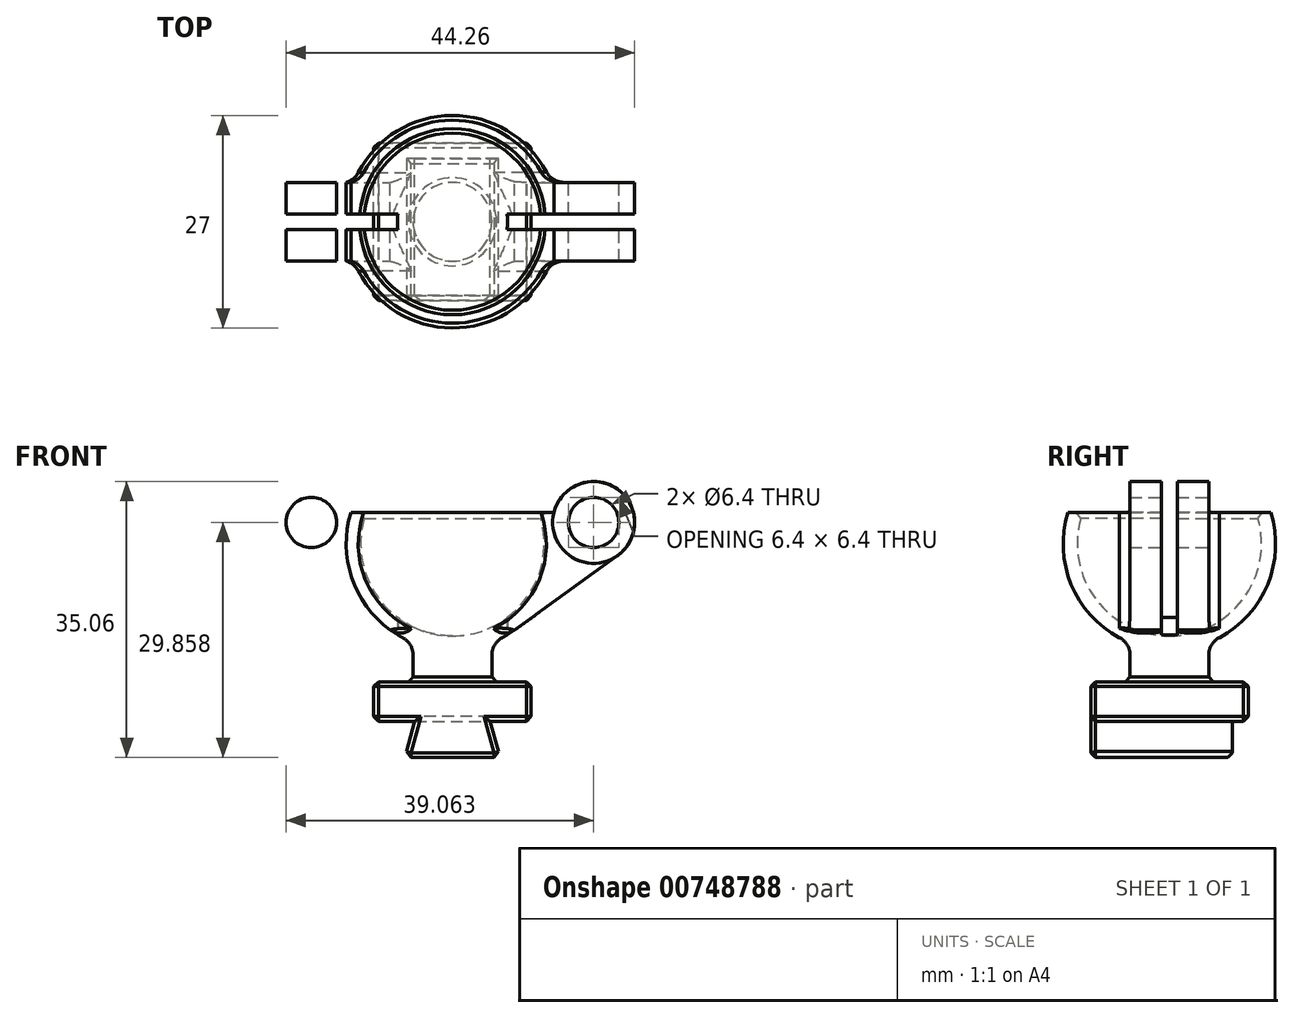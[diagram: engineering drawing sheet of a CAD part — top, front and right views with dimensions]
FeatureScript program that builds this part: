
annotation { "Feature Type Name" : "Feature", "Feature Type Description" : "" }
export const myFeature = defineFeature(function(context is Context, id is Id, definition is map)
    precondition{}
    {
        {
            assignVariable(context, id + "F0", {"name" : "BallWallThickness", "anyValue" : 2});
        }
        {
            assignVariable(context, id + "F1", {"name" : "DovetailBackstopDepth", "anyValue" : 2});
        }
        {
            assignVariable(context, id + "F2", {"name" : "DovetailHeight", "anyValue" : 5});
        }
        {
            assignVariable(context, id + "F3", {"name" : "Thickness", "anyValue" : 20});
        }
        {
            var Q0;
            Q0=qCreatedBy(makeId("Front.planeOp"),FACE);
            var sketch = newSketch(context, id + "F4", { "sketchPlane" : qUnion([Q0])});
            skLineSegment(sketch, "E0", {"start": v(20, 0) * mm, "end": v(20, 5) * mm});
            skLineSegment(sketch, "E1", {"start": v(20, 5) * mm, "end": v(0, 5) * mm});
            skLineSegment(sketch, "E2", {"start": v(5, 5) * mm, "end": v(5, 10) * mm});
            skLineSegment(sketch, "E3", {"start": v(5, 10) * mm, "end": v(15, 10) * mm});
            skLineSegment(sketch, "E4", {"start": v(15, 10) * mm, "end": v(15, 5) * mm});
            skLineSegment(sketch, "E5", {"start": v(10, 5) * mm, "end": v(10, -4.6) * mm, "construction": true});
            skArc(sketch, "E6", {"start": v(-2.9, 26.54) * mm, "mid": v(-2.18, 16.73) * mm, "end": v(5, 10) * mm});
            skPoint(sketch, "E6.centerSnap0", {"position": v(10, 10) * mm});
            skArc(sketch, "E7.trimOffspring", {"start": v(15, 10) * mm, "mid": v(22.18, 16.73) * mm, "end": v(22.9, 26.54) * mm});
            skLineSegment(sketch, "E8", {"start": v(10, 26.54) * mm, "end": v(10, 5) * mm});
            skArc(sketch, "E9", {"start": v(-1, 26.54) * mm, "mid": v(10, 10.84) * mm, "end": v(21, 26.54) * mm});
            skLineSegment(sketch, "E10", {"start": v(5.2, 0) * mm, "end": v(3.97, -4.6) * mm});
            skLineSegment(sketch, "E11", {"start": v(3.97, -4.6) * mm, "end": v(16.03, -4.6) * mm});
            skLineSegment(sketch, "E12.MirrorCS", {"start": v(14.8, 0) * mm, "end": v(16.03, -4.6) * mm});
            skLineSegment(sketch, "E13", {"start": v(14.8, 0) * mm, "end": v(20, 0) * mm});
            skLineSegment(sketch, "E14", {"start": v(5.2, 0) * mm, "end": v(0, 0) * mm});
            skLineSegment(sketch, "E15", {"start": v(0, 0) * mm, "end": v(0, 5) * mm});
            skLineSegment(sketch, "E16", {"start": v(-3.5, 22.54) * mm, "end": v(23.5, 22.54) * mm, "construction": true});
            skLineSegment(sketch, "E17", {"start": v(22.9, 26.54) * mm, "end": v(-2.9, 26.54) * mm});
            skLineSegment(sketch, "E18", {"start": v(5.2, 0) * mm, "end": v(14.8, 0) * mm});
            skCircle(sketch, "E19", {"center": v(27.93, 25.26) * mm, "radius": 3.2 * mm});
            skArc(sketch, "E20.0", {"start": v(30.98, 21.04) * mm, "mid": v(30.86, 29.56) * mm, "end": v(22.9, 26.54) * mm});
            skLineSegment(sketch, "E21", {"start": v(30.98, 21.04) * mm, "end": v(17.9, 11.6) * mm});
            skCircle(sketch, "E22.MirrorC", {"center": v(-7.93, 25.26) * mm, "radius": 3.2 * mm});
            skLineSegment(sketch, "E23.MirrorCS", {"start": v(-10.98, 21.04) * mm, "end": v(2.1, 11.6) * mm});
            skArc(sketch, "E24.MirrorCS", {"start": v(-10.98, 21.04) * mm, "mid": v(-10.86, 29.56) * mm, "end": v(-2.9, 26.54) * mm});
            skLineSegment(sketch, "E25", {"start": v(17.9, 11.6) * mm, "end": v(16.85, 13.06) * mm});
            skLineSegment(sketch, "E26.MirrorCS", {"start": v(2.1, 11.6) * mm, "end": v(3.15, 13.06) * mm});
            skSolve(sketch);
        }
        {
            var Q0;
            Q0=makeQuery(id+"F4.imprint","IMPRINT",FACE,{"disambiguationData":[TD([[makeQuery(id+"F4.imprint","IMPRINT",EDGE,{"derivedFrom":sQuery(id+"F4.wireOp",EDGE,"E10")}),1.0]])]});
            extrude(context, id + "F5", {"entities" : qUnion([Q0]), "depth" : (getVariable(context, 'Thickness') / 2) * mm, "hasSecondDirection" : true, "secondDirectionOppositeDirection" : true, "secondDirectionDepth" : (getVariable(context, 'Thickness') / 2 - getVariable(context, 'DovetailBackstopDepth')) * mm});
        }
        {
            var Q0;
            {var subQ4=sQuery(id+"F4.wireOp",EDGE,"E0");Q0=makeQuery(id+"F4.imprint","IMPRINT",FACE,{"disambiguationData":[TD([[makeQuery(id+"F4.imprint","IMPRINT",EDGE,{"derivedFrom":subQ4}),1.0]])]});}
            extrude(context, id + "F6", {"entities" : qUnion([Q0]), "operationType" : NewBodyOperationType.ADD, "depth" : (getVariable(context, 'Thickness')) * mm, "symmetric" : true});
        }
        {
            var Q0;
            {var subQ0=sQuery(id+"F4.wireOp",EDGE,"E2");Q0=makeQuery(id+"F4.imprint","IMPRINT",FACE,{"disambiguationData":[TD([[makeQuery(id+"F4.imprint","IMPRINT",EDGE,{"derivedFrom":subQ0}),-1.0]])]});}
            var Q1;
            Q1=sQuery(id+"F4.wireOp",EDGE,"E8");
            revolve(context, id + "F7", {"operationType" : NewBodyOperationType.ADD, "entities" : qUnion([Q0]), "axis" : qUnion([Q1]), "revolveType" : RevolveType.FULL});
        }
        {
            var Q0;
            Q0=makeQuery(id+"F7.opRevolve","SWEPT_FACE",FACE,{"disambiguationData":[OSD([sQuery(id+"F4.wireOp",EDGE,"E3")])]});
            var sketch = newSketch(context, id + "F8", { "sketchPlane" : qUnion([Q0])});
            skCircle(sketch, "E27", {"center": v(10, 0) * mm, "radius": 13.5 * mm});
            skCircle(sketch, "E28.0", {"center": v(10, 0) * mm, "radius": 5 * mm});
            skLineSegment(sketch, "E29", {"start": v(10, 13.5) * mm, "end": v(10, -13.5) * mm, "construction": true});
            skLineSegment(sketch, "E30", {"start": v(9.5, 13.5) * mm, "end": v(9.5, 6.98) * mm, "construction": true});
            skLineSegment(sketch, "E31.MirrorCS", {"start": v(10.5, 13.5) * mm, "end": v(10.5, 6.98) * mm, "construction": true});
            skLineSegment(sketch, "E32.trimOffspring", {"start": v(9.5, -6.98) * mm, "end": v(9.5, -13.5) * mm, "construction": true});
            skLineSegment(sketch, "E33.trimOffspring", {"start": v(10.5, -6.98) * mm, "end": v(10.5, -13.5) * mm, "construction": true});
            skLineSegment(sketch, "E34", {"start": v(-3.5, 0) * mm, "end": v(23.5, 0) * mm, "construction": true});
            skLineSegment(sketch, "E35", {"start": v(-3.46, 1) * mm, "end": v(3.07, 1) * mm});
            skLineSegment(sketch, "E36.MirrorCS", {"start": v(-3.46, -1) * mm, "end": v(3.07, -1) * mm});
            skLineSegment(sketch, "E37.trimOffspring", {"start": v(16.93, -1) * mm, "end": v(23.46, -1) * mm});
            skLineSegment(sketch, "E38.trimOffspring", {"start": v(16.93, 1) * mm, "end": v(23.46, 1) * mm});
            skCircle(sketch, "E39.0", {"center": v(10, 0) * mm, "radius": 7 * mm});
            skLineSegment(sketch, "E40", {"start": v(-3.46, -1) * mm, "end": v(-33.46, -1) * mm});
            skLineSegment(sketch, "E41", {"start": v(-33.46, -1) * mm, "end": v(-33.46, 1) * mm});
            skLineSegment(sketch, "E42", {"start": v(-33.46, 1) * mm, "end": v(-3.46, 1) * mm});
            skLineSegment(sketch, "E43.MirrorCS", {"start": v(53.46, 1) * mm, "end": v(23.46, 1) * mm});
            skLineSegment(sketch, "E44.MirrorCS", {"start": v(23.46, -1) * mm, "end": v(53.46, -1) * mm});
            skLineSegment(sketch, "E45.MirrorCS", {"start": v(53.46, -1) * mm, "end": v(53.46, 1) * mm});
            skSolve(sketch);
        }
        {
            var Q0;
            {var subQ6=sQuery(id+"F4.wireOp",EDGE,"E6");Q0=makeQuery(id+"F4.imprint","IMPRINT",FACE,{"disambiguationData":[TD([[makeQuery(id+"F4.imprint","IMPRINT",EDGE,{"derivedFrom":subQ6}),1.0]])]});}
            var Q1;
            {var subQ0=sQuery(id+"F4.wireOp",EDGE,"E26.MirrorCS");Q1=makeQuery(id+"F4.imprint","IMPRINT",FACE,{"disambiguationData":[TD([[makeQuery(id+"F4.imprint","IMPRINT",EDGE,{"derivedFrom":subQ0}),-1.0]])]});}
            var Q2;
            Q2=sQuery(id+"F4.wireOp",EDGE,"E8");
            revolve(context, id + "F9", {"operationType" : NewBodyOperationType.ADD, "entities" : qUnion([Q0, Q1]), "axis" : qUnion([Q2]), "revolveType" : RevolveType.FULL});
        }
        {
            var Q0;
            Q0=makeQuery(id+"F4.imprint","IMPRINT",FACE,{"disambiguationData":[TD([[makeQuery(id+"F4.imprint","IMPRINT",EDGE,{"derivedFrom":sQuery(id+"F4.wireOp",EDGE,"E22.MirrorC")}),1.0]])]});
            var Q1;
            {var subQ3=sQuery(id+"F4.wireOp",EDGE,"E26.MirrorCS");Q1=makeQuery(id+"F4.imprint","IMPRINT",FACE,{"disambiguationData":[TD([[makeQuery(id+"F4.imprint","IMPRINT",EDGE,{"derivedFrom":subQ3}),1.0]])]});}
            var Q2;
            {var subQ3=sQuery(id+"F4.wireOp",EDGE,"E25");Q2=makeQuery(id+"F4.imprint","IMPRINT",FACE,{"disambiguationData":[TD([[makeQuery(id+"F4.imprint","IMPRINT",EDGE,{"derivedFrom":subQ3}),-1.0]])]});}
            var Q3;
            Q3=makeQuery(id+"F4.imprint","IMPRINT",FACE,{"disambiguationData":[TD([[makeQuery(id+"F4.imprint","IMPRINT",EDGE,{"derivedFrom":sQuery(id+"F4.wireOp",EDGE,"E19")}),-1.0]])]});
            extrude(context, id + "F10", {"entities" : qUnion([Q0, Q1, Q2, Q3]), "operationType" : NewBodyOperationType.ADD, "depth" : (getVariable(context, 'BallWallThickness') + 8) * mm, "symmetric" : true});
        }
        {
            var Q0;
            {var subQ0=sQuery(id+"F8.wireOp",EDGE,"E35");Q0=makeQuery(id+"F8.imprint","IMPRINT",FACE,{"disambiguationData":[TD([[makeQuery(id+"F8.imprint","IMPRINT",EDGE,{"derivedFrom":subQ0}),-1.0]])]});}
            var Q1;
            {var subQ0=sQuery(id+"F8.wireOp",EDGE,"E32.trimOffspring");Q1=makeQuery(id+"F8.imprint","IMPRINT",FACE,{"disambiguationData":[TD([[makeQuery(id+"F8.imprint","IMPRINT",EDGE,{"derivedFrom":subQ0}),1.0]])]});}
            var Q2;
            {var subQ0=sQuery(id+"F8.wireOp",EDGE,"E37.trimOffspring");Q2=makeQuery(id+"F8.imprint","IMPRINT",FACE,{"disambiguationData":[TD([[makeQuery(id+"F8.imprint","IMPRINT",EDGE,{"derivedFrom":subQ0}),1.0]])]});}
            var Q3;
            {var subQ0=sQuery(id+"F8.wireOp",EDGE,"E30");Q3=makeQuery(id+"F8.imprint","IMPRINT",FACE,{"disambiguationData":[TD([[makeQuery(id+"F8.imprint","IMPRINT",EDGE,{"derivedFrom":subQ0}),1.0]])]});}
            var Q4;
            {var subQ2=sQuery(id+"F8.wireOp",EDGE,"E40");Q4=makeQuery(id+"F8.imprint","IMPRINT",FACE,{"disambiguationData":[TD([[makeQuery(id+"F8.imprint","IMPRINT",EDGE,{"derivedFrom":subQ2}),-1.0]])]});}
            var Q5;
            {var subQ2=sQuery(id+"F8.wireOp",EDGE,"E43.MirrorCS");Q5=makeQuery(id+"F8.imprint","IMPRINT",FACE,{"disambiguationData":[TD([[makeQuery(id+"F8.imprint","IMPRINT",EDGE,{"derivedFrom":subQ2}),1.0]])]});}
            extrude(context, id + "F11", {"entities" : qUnion([Q0, Q1, Q2, Q3, Q4, Q5]), "operationType" : NewBodyOperationType.REMOVE, "depth" : 25 * mm});
        }
        {
            var Q0;
            {var subQ0=sQuery(id+"F4.wireOp",EDGE,"E6");var subQ1=sQuery(id+"F4.wireOp",EDGE,"E3");var subQ2=sQuery(id+"F4.wireOp",EDGE,"E2");Q0=makeQuery(id+"F9.boolean.opBoolean","MERGE",EDGE,{"derivedFrom":[makeQuery(id+"F7.opRevolve","SWEPT_EDGE",EDGE,{"disambiguationData":[OSD([subQ2,subQ1,subQ0])]}),makeQuery(id+"F9.opRevolve","SWEPT_EDGE",EDGE,{"disambiguationData":[OSD([subQ2,subQ1,subQ0])]})]});}
            var Q1;
            Q1=makeQuery(id+"F7.opRevolve","SWEPT_EDGE",EDGE,{"disambiguationData":[OSD([sQuery(id+"F4.wireOp",EDGE,"E1"),sQuery(id+"F4.wireOp",EDGE,"E2")])]});
            var Q2;
            Q2=makeQuery(id+"F10.boolean.opBoolean","INTERSECT",EDGE,{"disambiguationData":[OD(1.0)],"derivedFrom":[makeQuery(id+"F9.opRevolve","SWEPT_FACE",FACE,{"disambiguationData":[OSD([sQuery(id+"F4.wireOp",EDGE,"E6")])]}),makeQuery(id+"F10.opExtrude","SWEPT_FACE",FACE,{"disambiguationData":[OSD([sQuery(id+"F4.wireOp",EDGE,"E26.MirrorCS")])]})]});
            var Q3;
            Q3=makeQuery(id+"F10.boolean.opBoolean","INTERSECT",EDGE,{"disambiguationData":[OD(1.0)],"derivedFrom":[makeQuery(id+"F9.opRevolve","SWEPT_FACE",FACE,{"disambiguationData":[OSD([sQuery(id+"F4.wireOp",EDGE,"E6")])]}),makeQuery(id+"F10.opExtrude","SWEPT_FACE",FACE,{"disambiguationData":[OSD([sQuery(id+"F4.wireOp",EDGE,"E25")])]})]});
            var Q4;
            Q4=makeQuery(id+"F10.boolean.opBoolean","INTERSECT",EDGE,{"disambiguationData":[OD(0.0)],"derivedFrom":[makeQuery(id+"F9.opRevolve","SWEPT_FACE",FACE,{"disambiguationData":[OSD([sQuery(id+"F4.wireOp",EDGE,"E6")])]}),makeQuery(id+"F10.opExtrude","SWEPT_FACE",FACE,{"disambiguationData":[OSD([sQuery(id+"F4.wireOp",EDGE,"E25")])]})]});
            var Q5;
            Q5=makeQuery(id+"F10.boolean.opBoolean","INTERSECT",EDGE,{"disambiguationData":[OD(0.0)],"derivedFrom":[makeQuery(id+"F9.opRevolve","SWEPT_FACE",FACE,{"disambiguationData":[OSD([sQuery(id+"F4.wireOp",EDGE,"E6")])]}),makeQuery(id+"F10.opExtrude","SWEPT_FACE",FACE,{"disambiguationData":[OSD([sQuery(id+"F4.wireOp",EDGE,"E26.MirrorCS")])]})]});
            var Q6;
            Q6=makeQuery(id+"F10.boolean.opBoolean","INTERSECT",EDGE,{"derivedFrom":[makeQuery(id+"F9.opRevolve","SWEPT_FACE",FACE,{"disambiguationData":[OSD([sQuery(id+"F4.wireOp",EDGE,"E6")])]}),makeQuery(id+"F10.opExtrude","CAP_FACE",FACE,{"disambiguationData":[OSD([sQuery(id+"F4.wireOp",EDGE,"E9"),sQuery(id+"F4.wireOp",EDGE,"E17"),sQuery(id+"F4.wireOp",EDGE,"E19"),sQuery(id+"F4.wireOp",EDGE,"E20.0"),sQuery(id+"F4.wireOp",EDGE,"E21"),sQuery(id+"F4.wireOp",EDGE,"E25")])],"isStart":false})]});
            var Q7;
            Q7=makeQuery(id+"F10.boolean.opBoolean","INTERSECT",EDGE,{"derivedFrom":[makeQuery(id+"F9.opRevolve","SWEPT_FACE",FACE,{"disambiguationData":[OSD([sQuery(id+"F4.wireOp",EDGE,"E6")])]}),makeQuery(id+"F10.opExtrude","CAP_FACE",FACE,{"disambiguationData":[OSD([sQuery(id+"F4.wireOp",EDGE,"E9"),sQuery(id+"F4.wireOp",EDGE,"E17"),sQuery(id+"F4.wireOp",EDGE,"E22.MirrorC"),sQuery(id+"F4.wireOp",EDGE,"E23.MirrorCS"),sQuery(id+"F4.wireOp",EDGE,"E24.MirrorCS"),sQuery(id+"F4.wireOp",EDGE,"E26.MirrorCS")])],"isStart":false})]});
            var Q8;
            Q8=makeQuery(id+"F10.boolean.opBoolean","INTERSECT",EDGE,{"derivedFrom":[makeQuery(id+"F9.opRevolve","SWEPT_FACE",FACE,{"disambiguationData":[OSD([sQuery(id+"F4.wireOp",EDGE,"E6")])]}),makeQuery(id+"F10.opExtrude","CAP_FACE",FACE,{"disambiguationData":[OSD([sQuery(id+"F4.wireOp",EDGE,"E9"),sQuery(id+"F4.wireOp",EDGE,"E17"),sQuery(id+"F4.wireOp",EDGE,"E22.MirrorC"),sQuery(id+"F4.wireOp",EDGE,"E23.MirrorCS"),sQuery(id+"F4.wireOp",EDGE,"E24.MirrorCS"),sQuery(id+"F4.wireOp",EDGE,"E26.MirrorCS")])],"isStart":true})]});
            var Q9;
            Q9=makeQuery(id+"F10.boolean.opBoolean","INTERSECT",EDGE,{"derivedFrom":[makeQuery(id+"F9.opRevolve","SWEPT_FACE",FACE,{"disambiguationData":[OSD([sQuery(id+"F4.wireOp",EDGE,"E6")])]}),makeQuery(id+"F10.opExtrude","CAP_FACE",FACE,{"disambiguationData":[OSD([sQuery(id+"F4.wireOp",EDGE,"E9"),sQuery(id+"F4.wireOp",EDGE,"E17"),sQuery(id+"F4.wireOp",EDGE,"E19"),sQuery(id+"F4.wireOp",EDGE,"E20.0"),sQuery(id+"F4.wireOp",EDGE,"E21"),sQuery(id+"F4.wireOp",EDGE,"E25")])],"isStart":true})]});
            fillet(context, id + "F12", {"entities" : qUnion([Q0, Q1, Q2, Q3, Q4, Q5, Q6, Q7, Q8, Q9]), "radius" : (getVariable(context, 'DovetailHeight') / 2) * mm, "tangentPropagation" : true, "allowEdgeOverflow" : false});
        }
        {
            var Q0;
            {var subQ0=sQuery(id+"F4.wireOp",EDGE,"E18");Q0=makeQuery(id+"F6.boolean.opBoolean","MERGE",FACE,{"derivedFrom":[makeQuery(id+"F5.opExtrude","CAP_FACE",FACE,{"disambiguationData":[OSD([sQuery(id+"F4.wireOp",EDGE,"E10"),sQuery(id+"F4.wireOp",EDGE,"E11"),sQuery(id+"F4.wireOp",EDGE,"E12.MirrorCS"),subQ0])],"isStart":false}),makeQuery(id+"F6.opExtrude","CAP_FACE",FACE,{"disambiguationData":[OSD([sQuery(id+"F4.wireOp",EDGE,"E0"),sQuery(id+"F4.wireOp",EDGE,"E1"),sQuery(id+"F4.wireOp",EDGE,"E13"),sQuery(id+"F4.wireOp",EDGE,"E14"),sQuery(id+"F4.wireOp",EDGE,"E15"),subQ0])],"isStart":false})]});}
            var Q1;
            Q1=makeQuery(id+"F6.opExtrude","SWEPT_FACE",FACE,{"disambiguationData":[OSD([sQuery(id+"F4.wireOp",EDGE,"E15")])]});
            var Q2;
            Q2=makeQuery(id+"F6.opExtrude","CAP_FACE",FACE,{"disambiguationData":[OSD([sQuery(id+"F4.wireOp",EDGE,"E0"),sQuery(id+"F4.wireOp",EDGE,"E1"),sQuery(id+"F4.wireOp",EDGE,"E13"),sQuery(id+"F4.wireOp",EDGE,"E14"),sQuery(id+"F4.wireOp",EDGE,"E15"),sQuery(id+"F4.wireOp",EDGE,"E18")])],"isStart":true});
            var Q3;
            Q3=makeQuery(id+"F6.opExtrude","SWEPT_FACE",FACE,{"disambiguationData":[OSD([sQuery(id+"F4.wireOp",EDGE,"E0")])]});
            var Q4;
            Q4=makeQuery(id+"F5.opExtrude","SWEPT_FACE",FACE,{"disambiguationData":[OSD([sQuery(id+"F4.wireOp",EDGE,"E11")])]});
            var Q5;
            Q5=makeQuery(id+"F6.opExtrude","SWEPT_FACE",FACE,{"disambiguationData":[OSD([sQuery(id+"F4.wireOp",EDGE,"E1")])]});
            var Q6;
            {var subQ0=sQuery(id+"F4.wireOp",EDGE,"E9");var subQ1=sQuery(id+"F4.wireOp",EDGE,"E17");Q6=makeQuery(id+"F11.boolean.opBoolean","SPLIT",EDGE,{"disambiguationData":[TD([makeQuery(id+"F11.opExtrude","SWEPT_FACE",FACE,{"disambiguationData":[OSD([sQuery(id+"F8.wireOp",EDGE,"E30")])]})])],"derivedFrom":makeQuery(id+"F9.opRevolve","SWEPT_EDGE",EDGE,{"disambiguationData":[OSD([subQ0,subQ1])]})});}
            var Q7;
            {var subQ0=sQuery(id+"F4.wireOp",EDGE,"E9");var subQ1=sQuery(id+"F4.wireOp",EDGE,"E17");Q7=makeQuery(id+"F11.boolean.opBoolean","SPLIT",EDGE,{"disambiguationData":[TD([makeQuery(id+"F11.opExtrude","SWEPT_FACE",FACE,{"disambiguationData":[OSD([sQuery(id+"F8.wireOp",EDGE,"E32.trimOffspring")])]})])],"derivedFrom":makeQuery(id+"F9.opRevolve","SWEPT_EDGE",EDGE,{"disambiguationData":[OSD([subQ0,subQ1])]})});}
            var Q8;
            {var subQ0=sQuery(id+"F4.wireOp",EDGE,"E9");var subQ1=sQuery(id+"F4.wireOp",EDGE,"E17");Q8=makeQuery(id+"F11.boolean.opBoolean","SPLIT",EDGE,{"disambiguationData":[TD([makeQuery(id+"F11.opExtrude","SWEPT_FACE",FACE,{"disambiguationData":[OSD([sQuery(id+"F8.wireOp",EDGE,"E33.trimOffspring")])]})])],"derivedFrom":makeQuery(id+"F9.opRevolve","SWEPT_EDGE",EDGE,{"disambiguationData":[OSD([subQ0,subQ1])]})});}
            var Q9;
            {var subQ0=sQuery(id+"F4.wireOp",EDGE,"E9");var subQ1=sQuery(id+"F4.wireOp",EDGE,"E17");Q9=makeQuery(id+"F11.boolean.opBoolean","SPLIT",EDGE,{"disambiguationData":[TD([makeQuery(id+"F11.opExtrude","SWEPT_FACE",FACE,{"disambiguationData":[OSD([sQuery(id+"F8.wireOp",EDGE,"E31.MirrorCS")])]})])],"derivedFrom":makeQuery(id+"F9.opRevolve","SWEPT_EDGE",EDGE,{"disambiguationData":[OSD([subQ0,subQ1])]})});}
            var Q10;
            {var subQ0=sQuery(id+"F4.wireOp",EDGE,"E17");var subQ1=sQuery(id+"F4.wireOp",EDGE,"E9");Q10=makeQuery(id+"F11.boolean.opBoolean","SPLIT",EDGE,{"disambiguationData":[TD([makeQuery(id+"F11.opExtrude","SWEPT_FACE",FACE,{"disambiguationData":[OSD([sQuery(id+"F8.wireOp",EDGE,"E36.MirrorCS"),sQuery(id+"F8.wireOp",EDGE,"E40")])]})])],"derivedFrom":makeQuery(id+"F9.opRevolve","SWEPT_EDGE",EDGE,{"disambiguationData":[OSD([subQ1,subQ0])]})});}
            var Q11;
            {var subQ0=sQuery(id+"F4.wireOp",EDGE,"E17");var subQ1=sQuery(id+"F4.wireOp",EDGE,"E9");Q11=makeQuery(id+"F11.boolean.opBoolean","SPLIT",EDGE,{"disambiguationData":[TD([makeQuery(id+"F11.opExtrude","SWEPT_FACE",FACE,{"disambiguationData":[OSD([sQuery(id+"F8.wireOp",EDGE,"E35"),sQuery(id+"F8.wireOp",EDGE,"E42")])]})])],"derivedFrom":makeQuery(id+"F9.opRevolve","SWEPT_EDGE",EDGE,{"disambiguationData":[OSD([subQ1,subQ0])]})});}
            chamfer(context, id + "F13", {"entities" : qUnion([Q0, Q1, Q2, Q3, Q4, Q5, Q6, Q7, Q8, Q9, Q10, Q11]), "width" : 0.6 * mm, "tangentPropagation" : true});
        }
    });
